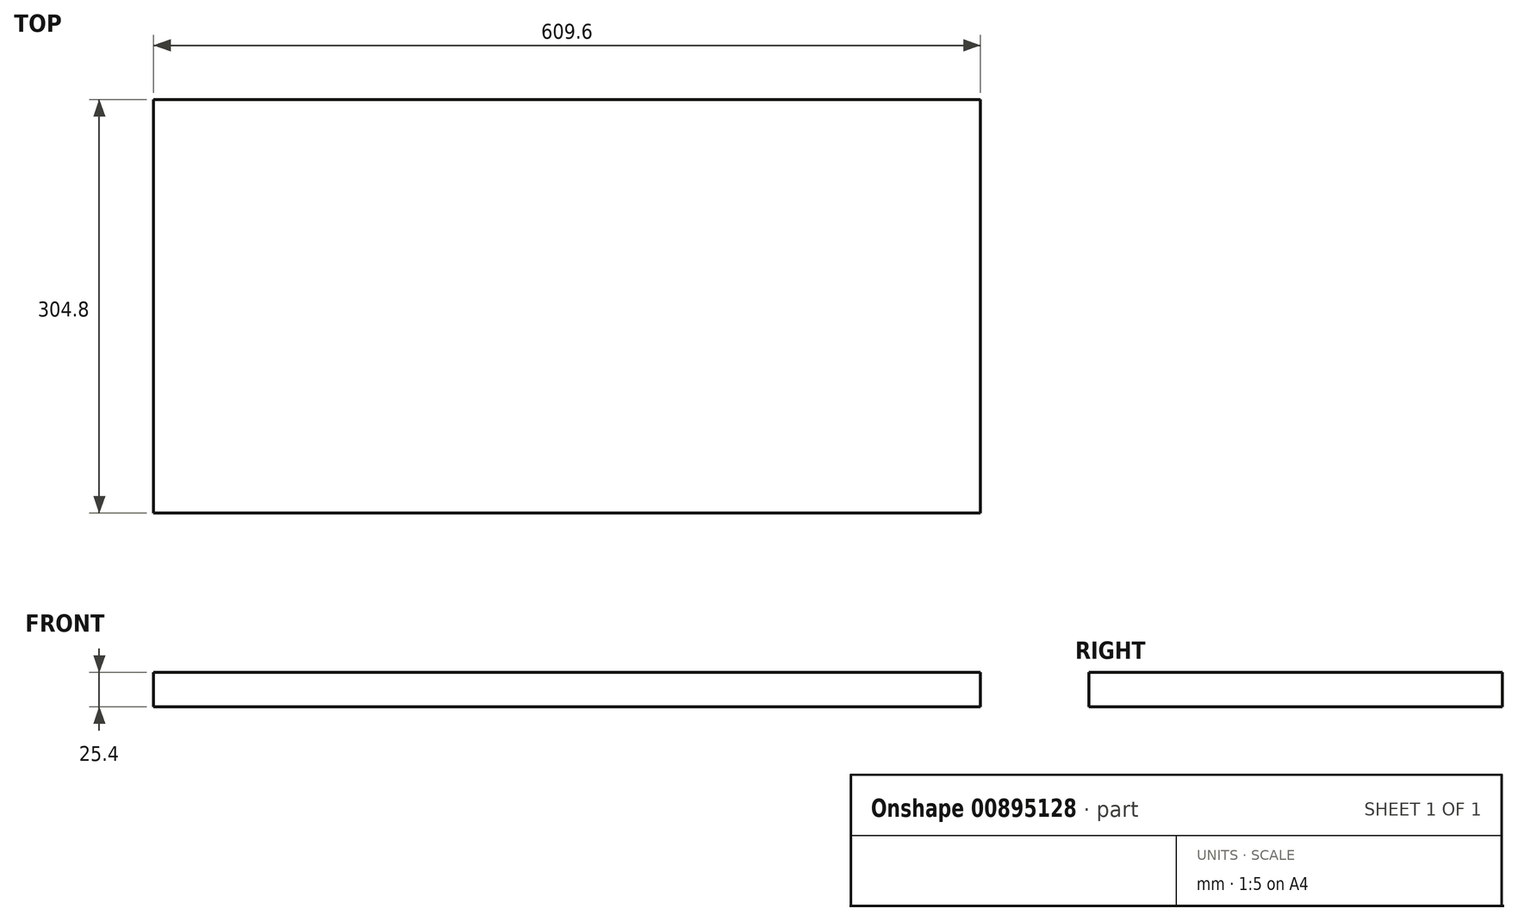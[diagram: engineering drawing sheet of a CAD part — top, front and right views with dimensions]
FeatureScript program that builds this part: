
annotation { "Feature Type Name" : "Feature", "Feature Type Description" : "" }
export const myFeature = defineFeature(function(context is Context, id is Id, definition is map)
    precondition{}
    {
        {
            var Q0;
            Q0=qCreatedBy(makeId("Top.planeOp"),FACE);
            var sketch = newSketch(context, id + "F0", { "sketchPlane" : qUnion([Q0])});
            skLineSegment(sketch, "E0.bottom", {"start": v(304.8, 152.4) * mm, "end": v(-304.8, 152.4) * mm});
            skLineSegment(sketch, "E0.top", {"start": v(304.8, -152.4) * mm, "end": v(-304.8, -152.4) * mm});
            skLineSegment(sketch, "E0.left", {"start": v(304.8, 152.4) * mm, "end": v(304.8, -152.4) * mm});
            skLineSegment(sketch, "E0.right", {"start": v(-304.8, 152.4) * mm, "end": v(-304.8, -152.4) * mm});
            skPoint(sketch, "E0.middle", {"position": v(0, 0) * mm});
            skSolve(sketch);
        }
        {
            var Q0;
            Q0=makeQuery(id+"F0.imprint","IMPRINT",FACE,{"disambiguationData":[TD([[makeQuery(id+"F0.imprint","IMPRINT",EDGE,{"derivedFrom":sQuery(id+"F0.wireOp",EDGE,"E0.bottom")}),1.0]])]});
            extrude(context, id + "F1", {"entities" : qUnion([Q0]), "depth" : 25.4 * mm, "offsetDistance" : 25.4 * mm});
        }
    });
